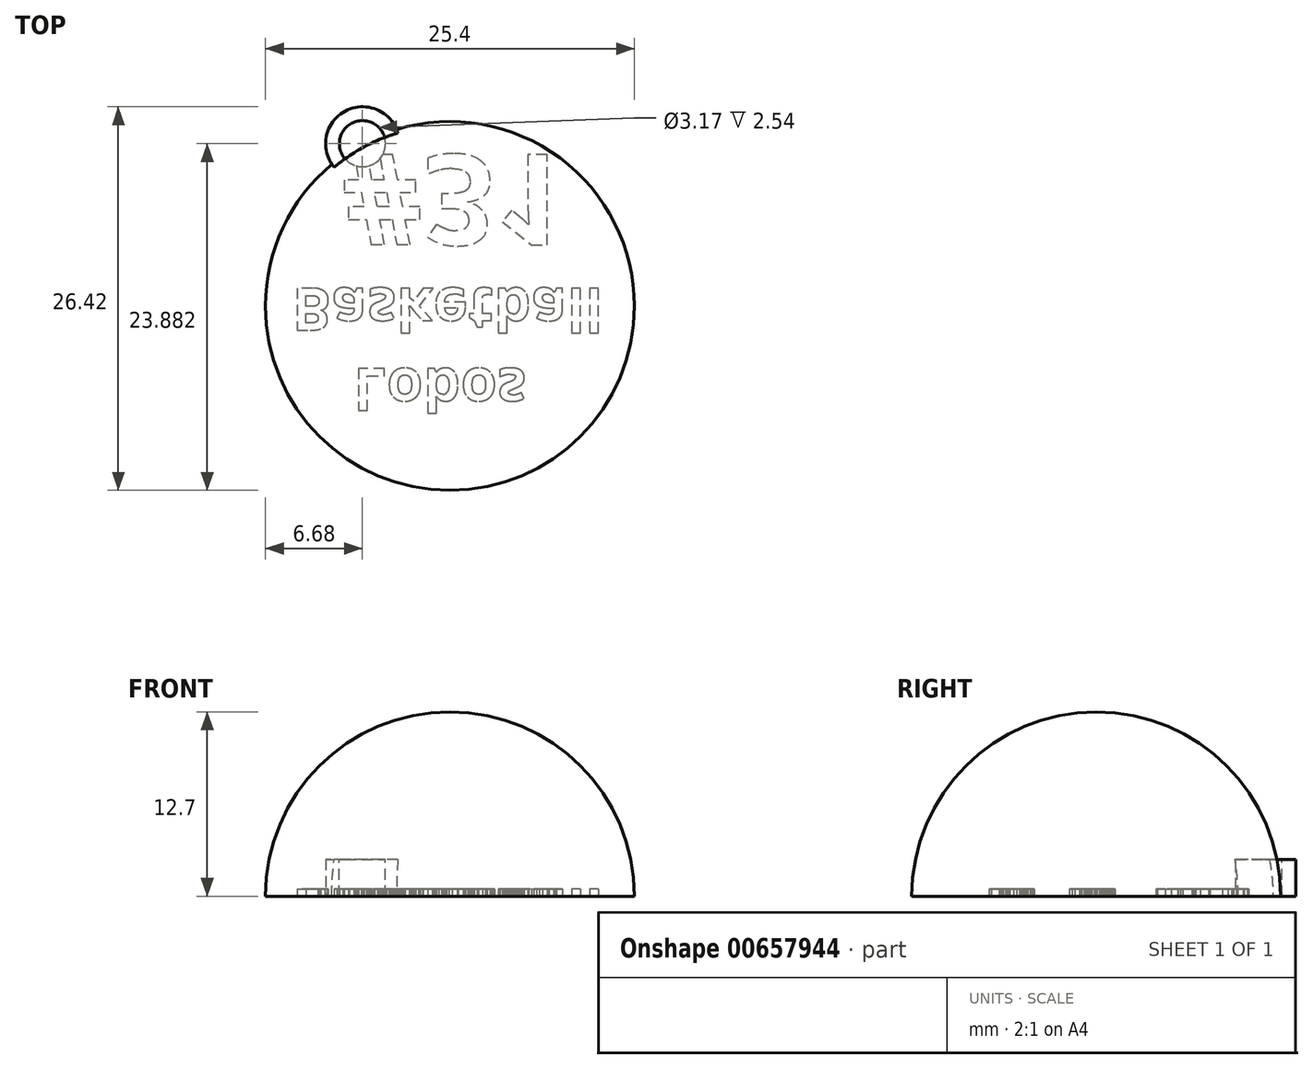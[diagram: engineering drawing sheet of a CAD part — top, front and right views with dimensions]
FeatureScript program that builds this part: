
annotation { "Feature Type Name" : "Feature", "Feature Type Description" : "" }
export const myFeature = defineFeature(function(context is Context, id is Id, definition is map)
    precondition{}
    {
        {
            var Q0;
            Q0=qCreatedBy(makeId("Top.planeOp"),FACE);
            var sketch = newSketch(context, id + "F0", { "sketchPlane" : qUnion([Q0])});
            skCircle(sketch, "E0", {"center": v(-6.02, 11.18) * mm, "radius": 2.54 * mm});
            skSolve(sketch);
        }
        {
            var Q0;
            Q0=qCreatedBy(makeId("Top.planeOp"),FACE);
            var sketch = newSketch(context, id + "F1", { "sketchPlane" : qUnion([Q0])});
            skArc(sketch, "E1", {"start": v(-12.7, 0) * mm, "mid": v(0, 12.7) * mm, "end": v(12.7, 0) * mm});
            skLineSegment(sketch, "E2", {"start": v(-12.7, 0) * mm, "end": v(12.7, 0) * mm});
            skSolve(sketch);
        }
        {
            var Q0;
            Q0 = qSketchRegion(id + "F1", true);
            var Q1;
            Q1=sQuery(id+"F1.wireOp",EDGE,"E2");
            revolve(context, id + "F2", {"entities" : qUnion([Q0]), "axis" : qUnion([Q1]), "revolveType" : RevolveType.ONE_DIRECTION, "angle" : 180 * degree});
        }
        {
            var Q0;
            Q0 = qSketchRegion(id + "F0", true);
            extrude(context, id + "F3", {"entities" : qUnion([Q0]), "operationType" : NewBodyOperationType.ADD, "depth" : 2.54 * mm, "offsetDistance" : 25.4 * mm});
        }
        {
            var Q0;
            Q0=makeQuery(id+"F3.opExtrude","CAP_FACE",FACE,{"disambiguationData":[OSD([sQuery(id+"F0.wireOp",EDGE,"E0")])],"isStart":false});
            var sketch = newSketch(context, id + "F4", { "sketchPlane" : qUnion([Q0])});
            skCircle(sketch, "E3", {"center": v(-6.02, 11.18) * mm, "radius": 1.59 * mm});
            skSolve(sketch);
        }
        {
            var Q0;
            Q0 = qSketchRegion(id + "F4", true);
            extrude(context, id + "F5", {"entities" : qUnion([Q0]), "operationType" : NewBodyOperationType.REMOVE, "oppositeDirection" : true, "depth" : 25.4 * mm, "offsetDistance" : 25.4 * mm});
        }
        {
            var Q0;
            Q0=makeQuery(id+"F3.boolean.opBoolean","MERGE",FACE,{"derivedFrom":[makeQuery(id+"F2.opRevolve","CAP_FACE",FACE,{"disambiguationData":[OSD([sQuery(id+"F1.wireOp",EDGE,"E1"),sQuery(id+"F1.wireOp",EDGE,"E2")])],"isStart":false}),makeQuery(id+"F3.opExtrude","CAP_FACE",FACE,{"disambiguationData":[OSD([sQuery(id+"F0.wireOp",EDGE,"E0")])],"isStart":true})]});
            var sketch = newSketch(context, id + "F6", { "sketchPlane" : qUnion([Q0])});
            skText(sketch, "E4", { "text": "     Lobos\n Basketball", "fontName": "OpenSans-Bold.ttf"});
            const initialGuessF6  = {"E4": [-0.01195, 0.0043, 1, 0, 0.00293]};
            skSetInitialGuess(sketch, initialGuessF6);
            skSolve(sketch);
        }
        {
            var Q0;
            Q0 = qSketchRegion(id + "F6", true);
            extrude(context, id + "F7", {"entities" : qUnion([Q0]), "operationType" : NewBodyOperationType.REMOVE, "oppositeDirection" : true, "depth" : 0.5 * mm, "offsetDistance" : 25.4 * mm});
        }
        {
            var Q0;
            {var subQ0=sQuery(id+"F1.wireOp",EDGE,"E1");var subQ1=sQuery(id+"F0.wireOp",EDGE,"E0");Q0=makeQuery(id+"F7.boolean.opBoolean","SPLIT",FACE,{"disambiguationData":[TD([makeQuery(id+"F2.opRevolve","SWEPT_FACE",FACE,{"disambiguationData":[OSD([subQ0])]})])],"derivedFrom":makeQuery(id+"F3.boolean.opBoolean","MERGE",FACE,{"derivedFrom":[makeQuery(id+"F2.opRevolve","CAP_FACE",FACE,{"disambiguationData":[OSD([subQ0,sQuery(id+"F1.wireOp",EDGE,"E2")])],"isStart":false}),makeQuery(id+"F3.opExtrude","CAP_FACE",FACE,{"disambiguationData":[OSD([subQ1])],"isStart":true})]})});}
            var sketch = newSketch(context, id + "F8", { "sketchPlane" : qUnion([Q0])});
            skText(sketch, "E5", { "text": "  #31", "fontName": "OpenSans-Bold.ttf"});
            const initialGuessF8  = {"E5": [-0.012, -0.01042, 1, 0, 0.00626]};
            skSetInitialGuess(sketch, initialGuessF8);
            skSolve(sketch);
        }
        {
            var Q0;
            Q0 = qSketchRegion(id + "F8", true);
            extrude(context, id + "F9", {"entities" : qUnion([Q0]), "operationType" : NewBodyOperationType.REMOVE, "oppositeDirection" : true, "depth" : 0.5 * mm, "offsetDistance" : 25.4 * mm});
        }
    });
